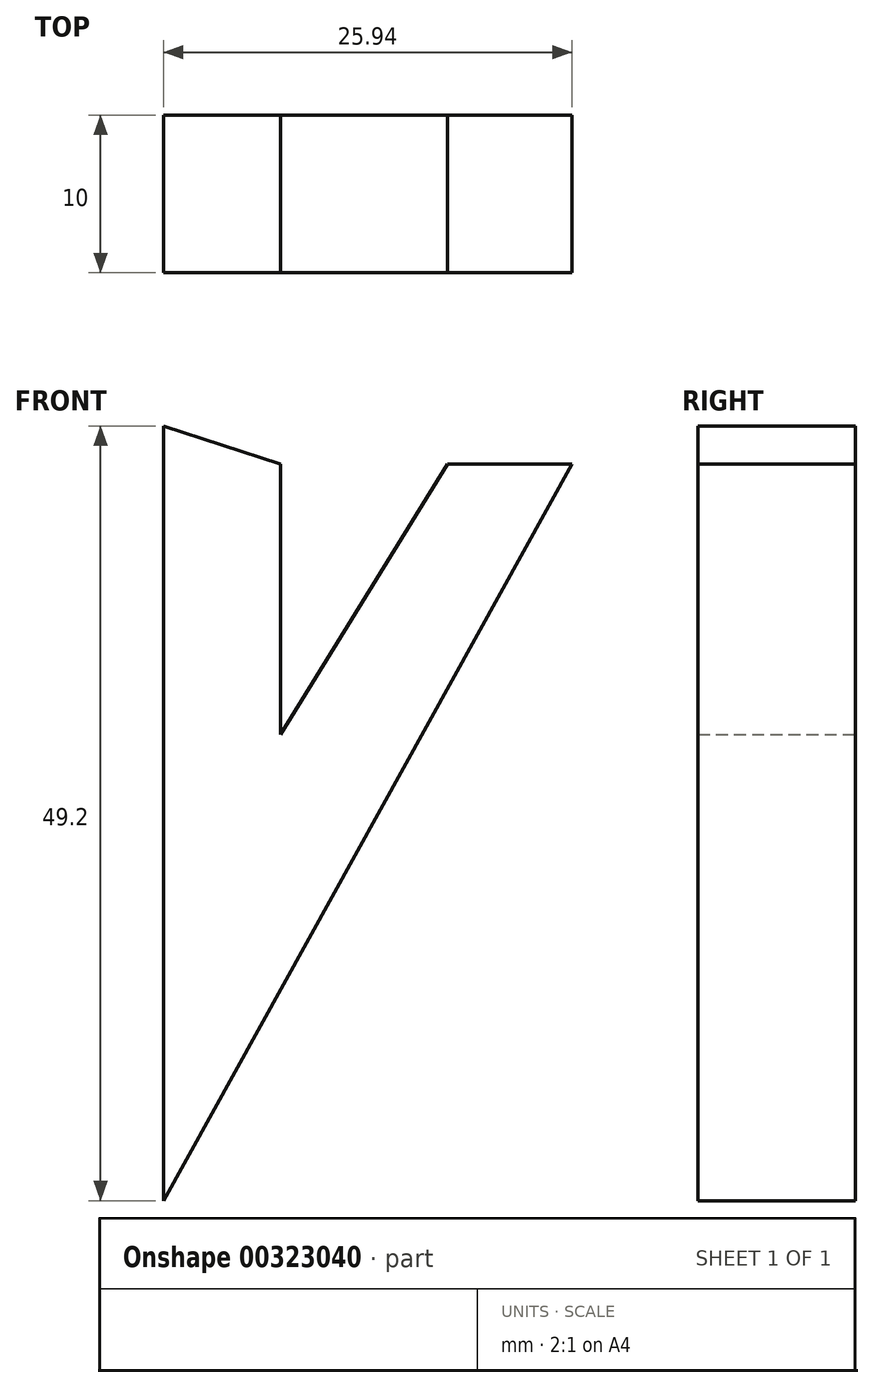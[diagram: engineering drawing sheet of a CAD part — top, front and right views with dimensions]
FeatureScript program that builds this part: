
annotation { "Feature Type Name" : "Feature", "Feature Type Description" : "" }
export const myFeature = defineFeature(function(context is Context, id is Id, definition is map)
    precondition{}
    {
        {
            var Q0;
            Q0=qCreatedBy(makeId("Front.planeOp"),FACE);
            var sketch = newSketch(context, id + "F0", { "sketchPlane" : qUnion([Q0])});
            skLineSegment(sketch, "E0", {"start": v(0, 0) * mm, "end": v(0, 49.2) * mm});
            skLineSegment(sketch, "E1", {"start": v(0, 0) * mm, "end": v(25.94, 46.8) * mm});
            skLineSegment(sketch, "E2", {"start": v(18.04, 46.8) * mm, "end": v(25.94, 46.8) * mm});
            skLineSegment(sketch, "E3", {"start": v(18.04, 46.8) * mm, "end": v(7.43, 29.6) * mm});
            skLineSegment(sketch, "E4", {"start": v(7.43, 29.6) * mm, "end": v(7.43, 46.8) * mm});
            skLineSegment(sketch, "E5", {"start": v(7.43, 46.8) * mm, "end": v(0, 49.2) * mm});
            skSolve(sketch);
        }
        {
            var Q0;
            Q0=makeQuery(id+"F0.imprint","IMPRINT",FACE,{"disambiguationData":[TD([[makeQuery(id+"F0.imprint","IMPRINT",EDGE,{"derivedFrom":sQuery(id+"F0.wireOp",EDGE,"E0")}),-1.0]])]});
            extrude(context, id + "F1", {"entities" : qUnion([Q0]), "depth" : 10 * mm});
        }
    });
